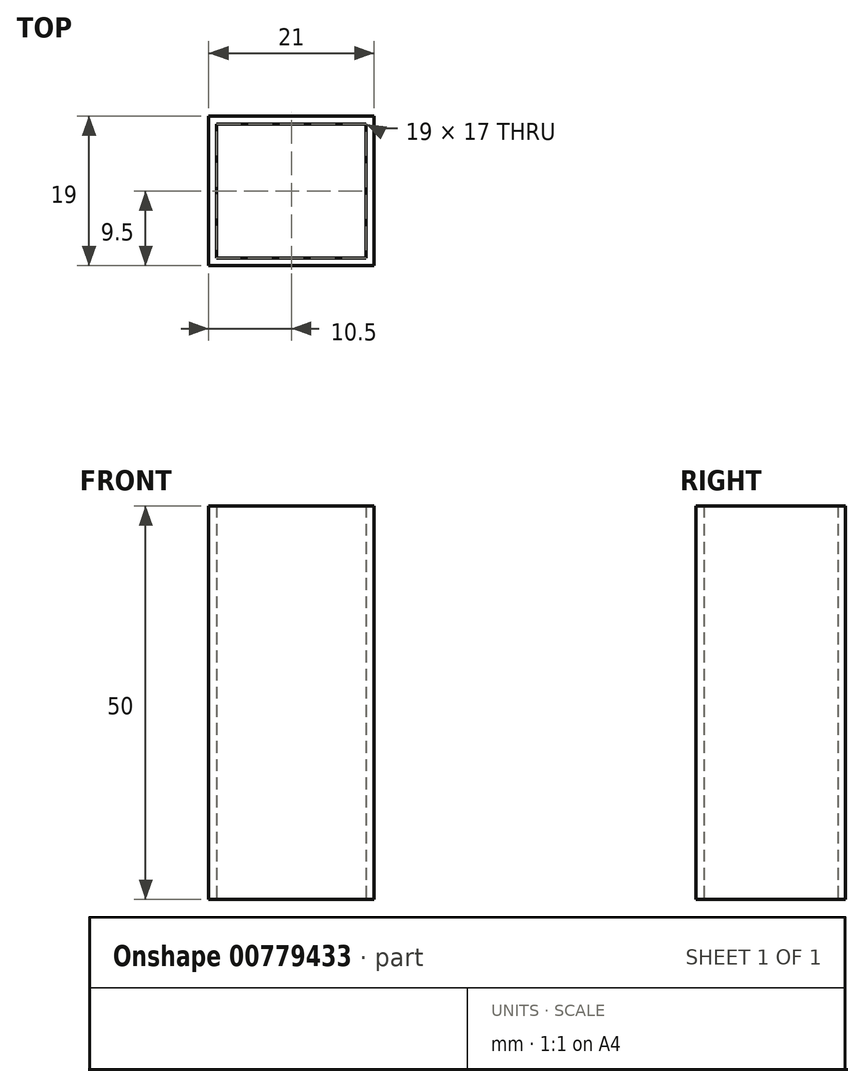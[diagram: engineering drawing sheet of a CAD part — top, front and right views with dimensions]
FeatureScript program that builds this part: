
annotation { "Feature Type Name" : "Feature", "Feature Type Description" : "" }
export const myFeature = defineFeature(function(context is Context, id is Id, definition is map)
    precondition{}
    {
        {
            var Q0;
            Q0=qCreatedBy(makeId("Top.planeOp"),FACE);
            var sketch = newSketch(context, id + "F0", { "sketchPlane" : qUnion([Q0])});
            skLineSegment(sketch, "E0.bottom", {"start": v(0, 0) * mm, "end": v(21, 0) * mm});
            skLineSegment(sketch, "E0.top", {"start": v(0, -19) * mm, "end": v(21, -19) * mm});
            skLineSegment(sketch, "E0.left", {"start": v(0, 0) * mm, "end": v(0, -19) * mm});
            skLineSegment(sketch, "E0.right", {"start": v(21, 0) * mm, "end": v(21, -19) * mm});
            skLineSegment(sketch, "E1.bottom", {"start": v(1, -1) * mm, "end": v(20, -1) * mm});
            skLineSegment(sketch, "E1.top", {"start": v(1, -18) * mm, "end": v(20, -18) * mm});
            skLineSegment(sketch, "E1.left", {"start": v(1, -1) * mm, "end": v(1, -18) * mm});
            skLineSegment(sketch, "E1.right", {"start": v(20, -1) * mm, "end": v(20, -18) * mm});
            skSolve(sketch);
        }
        {
            var Q0;
            Q0=makeQuery(id+"F0.imprint","IMPRINT",FACE,{"disambiguationData":[TD([[makeQuery(id+"F0.imprint","IMPRINT",EDGE,{"derivedFrom":sQuery(id+"F0.wireOp",EDGE,"E0.bottom")}),-1.0]])]});
            extrude(context, id + "F1", {"entities" : qUnion([Q0]), "depth" : 50 * mm, "offsetDistance" : 25 * mm});
        }
    });
